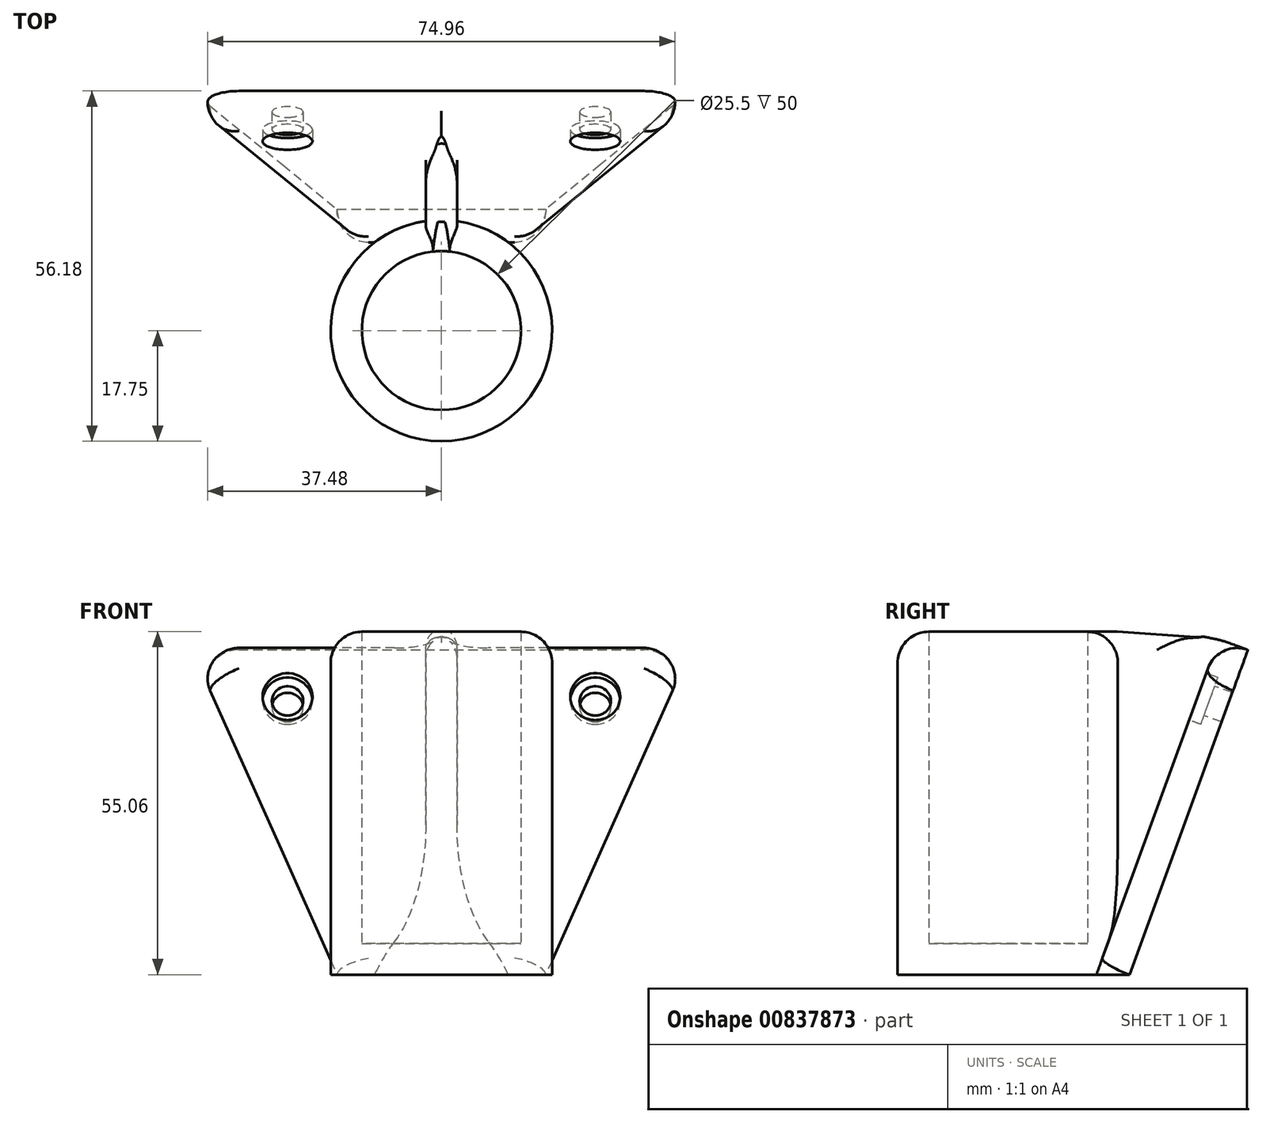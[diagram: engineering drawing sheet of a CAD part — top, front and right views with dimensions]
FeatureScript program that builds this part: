
annotation { "Feature Type Name" : "Feature", "Feature Type Description" : "" }
export const myFeature = defineFeature(function(context is Context, id is Id, definition is map)
    precondition{}
    {
        {
            var Q0;
            Q0=qCreatedBy(makeId("Top.planeOp"),FACE);
            var sketch = newSketch(context, id + "F0", { "sketchPlane" : qUnion([Q0])});
            skCircle(sketch, "E0", {"center": v(0, 0) * mm, "radius": 12.75 * mm});
            skCircle(sketch, "E1", {"center": v(0, 0) * mm, "radius": 17.75 * mm});
            skSolve(sketch);
        }
        {
            var Q0;
            Q0=makeQuery(id+"F0.imprint","IMPRINT",FACE,{"disambiguationData":[TD([[makeQuery(id+"F0.imprint","IMPRINT",EDGE,{"derivedFrom":sQuery(id+"F0.wireOp",EDGE,"E0")}),-1.0]])]});
            extrude(context, id + "F1", {"entities" : qUnion([Q0]), "depth" : 50 * mm, "offsetDistance" : 25 * mm});
        }
        {
            var Q0;
            Q0 = qSketchRegion(id + "F0", true);
            var Q1;
            Q1=makeQuery(id+"F0.imprint","IMPRINT",FACE,{"disambiguationData":[TD([[makeQuery(id+"F0.imprint","IMPRINT",EDGE,{"derivedFrom":sQuery(id+"F0.wireOp",EDGE,"E0")}),1.0]])]});
            extrude(context, id + "F2", {"entities" : qUnion([Q0, Q1]), "operationType" : NewBodyOperationType.ADD, "oppositeDirection" : true, "depth" : 5 * mm, "offsetDistance" : 25 * mm});
        }
        {
            var Q0;
            Q0=qCreatedBy(makeId("Right.planeOp"),FACE);
            var sketch = newSketch(context, id + "F3", { "sketchPlane" : qUnion([Q0])});
            skLineSegment(sketch, "E2.bottom", {"start": v(33.73, 48.81) * mm, "end": v(38.43, 47.1) * mm});
            skLineSegment(sketch, "E2.left", {"start": v(33.73, 48.81) * mm, "end": v(14.14, -5) * mm});
            skLineSegment(sketch, "E2.right", {"start": v(38.43, 47.1) * mm, "end": v(19.46, -5) * mm});
            skLineSegment(sketch, "E3", {"start": v(14.14, -5) * mm, "end": v(19.46, -5) * mm});
            skSolve(sketch);
        }
        {
            var Q0;
            Q0 = qSketchRegion(id + "F3", true);
            extrude(context, id + "F4", {"entities" : qUnion([Q0]), "operationType" : NewBodyOperationType.ADD, "oppositeDirection" : true, "depth" : 40 * mm, "offsetDistance" : 25 * mm, "hasSecondDirection" : true, "secondDirectionOppositeDirection" : false, "secondDirectionDepth" : 40 * mm});
        }
        {
            var Q0;
            Q0=qCreatedBy(makeId("Right.planeOp"),FACE);
            var sketch = newSketch(context, id + "F5", { "sketchPlane" : qUnion([Q0])});
            skLineSegment(sketch, "E4", {"start": v(17.47, 50.06) * mm, "end": v(17.47, 2.94) * mm});
            skLineSegment(sketch, "E5", {"start": v(17.47, 2.94) * mm, "end": v(34.07, 48.86) * mm});
            skLineSegment(sketch, "E6", {"start": v(34.07, 48.86) * mm, "end": v(17.47, 50.06) * mm});
            skSolve(sketch);
        }
        {
            var Q0;
            Q0 = qSketchRegion(id + "F5", true);
            extrude(context, id + "F6", {"entities" : qUnion([Q0]), "operationType" : NewBodyOperationType.ADD, "depth" : 2.5 * mm, "offsetDistance" : 25 * mm, "hasSecondDirection" : true, "secondDirectionOppositeDirection" : true, "secondDirectionDepth" : 2.5 * mm});
        }
        {
            var Q0;
            Q0=makeQuery(id+"F4.opExtrude","SWEPT_FACE",FACE,{"disambiguationData":[OSD([sQuery(id+"F3.wireOp",EDGE,"E2.right")])]});
            var sketch = newSketch(context, id + "F7", { "sketchPlane" : qUnion([Q0])});
            skLineSegment(sketch, "E7", {"start": v(-40, 57.4) * mm, "end": v(-16.73, 1.96) * mm});
            skLineSegment(sketch, "E8", {"start": v(-40, 1.96) * mm, "end": v(-40, 57.4) * mm});
            skLineSegment(sketch, "E9.MirrorCS", {"start": v(40, 57.4) * mm, "end": v(16.73, 1.96) * mm});
            skLineSegment(sketch, "E10.MirrorCS", {"start": v(40, 1.96) * mm, "end": v(40, 57.4) * mm});
            skLineSegment(sketch, "E11", {"start": v(-16.73, 1.96) * mm, "end": v(-16.73, -1.57) * mm});
            skLineSegment(sketch, "E12", {"start": v(-16.73, -1.57) * mm, "end": v(-40, -1.57) * mm});
            skLineSegment(sketch, "E13", {"start": v(-40, -1.57) * mm, "end": v(-40, 1.96) * mm});
            skLineSegment(sketch, "E14", {"start": v(16.73, 1.96) * mm, "end": v(16.73, -1.57) * mm});
            skLineSegment(sketch, "E15", {"start": v(16.73, -1.57) * mm, "end": v(40, -1.57) * mm});
            skLineSegment(sketch, "E16", {"start": v(40, -1.57) * mm, "end": v(40, 1.96) * mm});
            skSolve(sketch);
        }
        {
            var Q0;
            Q0 = qSketchRegion(id + "F7", true);
            extrude(context, id + "F8", {"entities" : qUnion([Q0]), "operationType" : NewBodyOperationType.REMOVE, "oppositeDirection" : true, "depth" : 6 * mm, "offsetDistance" : 25 * mm});
        }
        {
            var Q0;
            Q0=makeQuery(id+"F1.opExtrude","CAP_EDGE",EDGE,{"disambiguationData":[OSD([sQuery(id+"F0.wireOp",EDGE,"E1")])],"isStart":false});
            fillet(context, id + "F9", {"entities" : qUnion([Q0]), "radius" : 5 * mm, "tangentPropagation" : true, "allowEdgeOverflow" : false});
        }
        {
            var Q0;
            Q0=makeQuery(id+"F6.opExtrude","CAP_EDGE",EDGE,{"disambiguationData":[OSD([sQuery(id+"F5.wireOp",EDGE,"E6")])],"isStart":false});
            var Q1;
            Q1=makeQuery(id+"F6.opExtrude","CAP_EDGE",EDGE,{"disambiguationData":[OSD([sQuery(id+"F5.wireOp",EDGE,"E6")])],"isStart":true});
            fillet(context, id + "F10", {"entities" : qUnion([Q0, Q1]), "radius" : 2.5 * mm, "tangentPropagation" : true, "allowEdgeOverflow" : false});
        }
        {
            var Q0;
            Q0=makeQuery(id+"F6.boolean.opBoolean","INTERSECT",EDGE,{"derivedFrom":[makeQuery(id+"F4.opExtrude","SWEPT_FACE",FACE,{"disambiguationData":[OSD([sQuery(id+"F3.wireOp",EDGE,"E2.left")])]}),makeQuery(id+"F6.opExtrude","CAP_FACE",FACE,{"disambiguationData":[OSD([sQuery(id+"F5.wireOp",EDGE,"E4"),sQuery(id+"F5.wireOp",EDGE,"E5"),sQuery(id+"F5.wireOp",EDGE,"E6")])],"isStart":true})]});
            var Q1;
            Q1=makeQuery(id+"F6.boolean.opBoolean","INTERSECT",EDGE,{"derivedFrom":[makeQuery(id+"F4.opExtrude","SWEPT_FACE",FACE,{"disambiguationData":[OSD([sQuery(id+"F3.wireOp",EDGE,"E2.left")])]}),makeQuery(id+"F6.opExtrude","CAP_FACE",FACE,{"disambiguationData":[OSD([sQuery(id+"F5.wireOp",EDGE,"E4"),sQuery(id+"F5.wireOp",EDGE,"E5"),sQuery(id+"F5.wireOp",EDGE,"E6")])],"isStart":false})]});
            fillet(context, id + "F11", {"entities" : qUnion([Q0, Q1]), "radius" : 5 * mm, "tangentPropagation" : true, "allowEdgeOverflow" : false});
        }
        {
            var Q0;
            {var subQ3=sQuery(id+"F3.wireOp",EDGE,"E2.left");Q0=makeQuery(id+"F8.boolean.opBoolean","INTERSECT",EDGE,{"derivedFrom":[makeQuery(id+"F6.boolean.opBoolean","SPLIT",FACE,{"disambiguationData":[TD([makeQuery(id+"F6.opExtrude","CAP_FACE",FACE,{"disambiguationData":[OSD([sQuery(id+"F5.wireOp",EDGE,"E4"),sQuery(id+"F5.wireOp",EDGE,"E5"),sQuery(id+"F5.wireOp",EDGE,"E6")])],"isStart":false})])],"derivedFrom":makeQuery(id+"F4.opExtrude","SWEPT_FACE",FACE,{"disambiguationData":[OSD([subQ3])]})}),makeQuery(id+"F8.opExtrude","SWEPT_FACE",FACE,{"disambiguationData":[OSD([sQuery(id+"F7.wireOp",EDGE,"E11")])]})]});}
            var Q1;
            {var subQ3=sQuery(id+"F3.wireOp",EDGE,"E2.left");Q1=makeQuery(id+"F8.boolean.opBoolean","INTERSECT",EDGE,{"derivedFrom":[makeQuery(id+"F6.boolean.opBoolean","SPLIT",FACE,{"disambiguationData":[TD([makeQuery(id+"F6.opExtrude","CAP_FACE",FACE,{"disambiguationData":[OSD([sQuery(id+"F5.wireOp",EDGE,"E4"),sQuery(id+"F5.wireOp",EDGE,"E5"),sQuery(id+"F5.wireOp",EDGE,"E6")])],"isStart":false})])],"derivedFrom":makeQuery(id+"F4.opExtrude","SWEPT_FACE",FACE,{"disambiguationData":[OSD([subQ3])]})}),makeQuery(id+"F8.opExtrude","SWEPT_FACE",FACE,{"disambiguationData":[OSD([sQuery(id+"F7.wireOp",EDGE,"E7")])]})]});}
            var Q2;
            {var subQ3=sQuery(id+"F3.wireOp",EDGE,"E2.left");Q2=makeQuery(id+"F8.boolean.opBoolean","INTERSECT",EDGE,{"derivedFrom":[makeQuery(id+"F6.boolean.opBoolean","SPLIT",FACE,{"disambiguationData":[TD([makeQuery(id+"F6.opExtrude","CAP_FACE",FACE,{"disambiguationData":[OSD([sQuery(id+"F5.wireOp",EDGE,"E4"),sQuery(id+"F5.wireOp",EDGE,"E5"),sQuery(id+"F5.wireOp",EDGE,"E6")])],"isStart":true})])],"derivedFrom":makeQuery(id+"F4.opExtrude","SWEPT_FACE",FACE,{"disambiguationData":[OSD([subQ3])]})}),makeQuery(id+"F8.opExtrude","SWEPT_FACE",FACE,{"disambiguationData":[OSD([sQuery(id+"F7.wireOp",EDGE,"E14")])]})]});}
            var Q3;
            {var subQ3=sQuery(id+"F3.wireOp",EDGE,"E2.left");Q3=makeQuery(id+"F8.boolean.opBoolean","INTERSECT",EDGE,{"derivedFrom":[makeQuery(id+"F6.boolean.opBoolean","SPLIT",FACE,{"disambiguationData":[TD([makeQuery(id+"F6.opExtrude","CAP_FACE",FACE,{"disambiguationData":[OSD([sQuery(id+"F5.wireOp",EDGE,"E4"),sQuery(id+"F5.wireOp",EDGE,"E5"),sQuery(id+"F5.wireOp",EDGE,"E6")])],"isStart":true})])],"derivedFrom":makeQuery(id+"F4.opExtrude","SWEPT_FACE",FACE,{"disambiguationData":[OSD([subQ3])]})}),makeQuery(id+"F8.opExtrude","SWEPT_FACE",FACE,{"disambiguationData":[OSD([sQuery(id+"F7.wireOp",EDGE,"E9.MirrorCS")])]})]});}
            fillet(context, id + "F12", {"entities" : qUnion([Q0, Q1, Q2, Q3]), "radius" : 5 * mm, "tangentPropagation" : true, "allowEdgeOverflow" : false});
        }
        {
            var Q0;
            {var subQ0=sQuery(id+"F3.wireOp",EDGE,"E2.bottom");var subQ1=sQuery(id+"F3.wireOp",EDGE,"E2.left");Q0=makeQuery(id+"F6.boolean.opBoolean","SPLIT",EDGE,{"disambiguationData":[TD([makeQuery(id+"F6.opExtrude","CAP_FACE",FACE,{"disambiguationData":[OSD([sQuery(id+"F5.wireOp",EDGE,"E4"),sQuery(id+"F5.wireOp",EDGE,"E5"),sQuery(id+"F5.wireOp",EDGE,"E6")])],"isStart":true})])],"derivedFrom":makeQuery(id+"F4.opExtrude","SWEPT_EDGE",EDGE,{"disambiguationData":[OSD([subQ0,subQ1])]})});}
            var Q1;
            {var subQ0=sQuery(id+"F3.wireOp",EDGE,"E2.bottom");var subQ1=sQuery(id+"F3.wireOp",EDGE,"E2.left");Q1=makeQuery(id+"F6.boolean.opBoolean","SPLIT",EDGE,{"disambiguationData":[TD([makeQuery(id+"F6.opExtrude","CAP_FACE",FACE,{"disambiguationData":[OSD([sQuery(id+"F5.wireOp",EDGE,"E4"),sQuery(id+"F5.wireOp",EDGE,"E5"),sQuery(id+"F5.wireOp",EDGE,"E6")])],"isStart":false})])],"derivedFrom":makeQuery(id+"F4.opExtrude","SWEPT_EDGE",EDGE,{"disambiguationData":[OSD([subQ0,subQ1])]})});}
            fillet(context, id + "F13", {"entities" : qUnion([Q0, Q1]), "radius" : 5 * mm, "allowEdgeOverflow" : false});
        }
        {
            var Q0;
            {var subQ3=sQuery(id+"F3.wireOp",EDGE,"E2.left");Q0=makeQuery(id+"F6.boolean.opBoolean","SPLIT",FACE,{"disambiguationData":[TD([makeQuery(id+"F6.opExtrude","CAP_FACE",FACE,{"disambiguationData":[OSD([sQuery(id+"F5.wireOp",EDGE,"E4"),sQuery(id+"F5.wireOp",EDGE,"E5"),sQuery(id+"F5.wireOp",EDGE,"E6")])],"isStart":true})])],"derivedFrom":makeQuery(id+"F4.opExtrude","SWEPT_FACE",FACE,{"disambiguationData":[OSD([subQ3])]})});}
            var sketch = newSketch(context, id + "F14", { "sketchPlane" : qUnion([Q0])});
            skPoint(sketch, "E17", {"position": v(-24.67, 47.59) * mm});
            skPoint(sketch, "E18.MirrorP", {"position": v(24.67, 47.59) * mm});
            skSolve(sketch);
        }
        {
            var Q0;
            Q0=sQuery(id+"F14.wireOp",VERTEX,"E17");
            var Q1;
            Q1=sQuery(id+"F14.wireOp",VERTEX,"E18.MirrorP");
            var Q2;
            Q2=makeQuery(id+"F1.opExtrude","SWEPT_BODY",BODY,{"disambiguationData":[OSD([sQuery(id+"F0.wireOp",EDGE,"E0"),sQuery(id+"F0.wireOp",EDGE,"E1")])]});
            hole(context, id + "F15", {"style" : HoleStyle.C_BORE, "endStyle" : HoleEndStyle.THROUGH, "holeDiameter" : 5 * mm, "cBoreDiameter" : 8 * mm, "cBoreDepth" : 2 * mm, "majorDiameter" : 5 * mm, "isTappedThrough" : true, "tappedDepth" : 12 * mm, "tapClearance" : 3, "locations" : qUnion([Q0, Q1]), "scope" : qUnion([Q2])});
        }
        {
            var Q0;
            {var subQ0=sQuery(id+"F3.wireOp",EDGE,"E2.left");var subQ1=sQuery(id+"F3.wireOp",EDGE,"E2.bottom");Q0=makeQuery(id+"F13.opFillet","BLEND_EDGE",EDGE,{"blendedFrom":[makeQuery(id+"F6.boolean.opBoolean","SPLIT",EDGE,{"disambiguationData":[TD([makeQuery(id+"F6.opExtrude","CAP_FACE",FACE,{"disambiguationData":[OSD([sQuery(id+"F5.wireOp",EDGE,"E4"),sQuery(id+"F5.wireOp",EDGE,"E5"),sQuery(id+"F5.wireOp",EDGE,"E6")])],"isStart":true})])],"derivedFrom":makeQuery(id+"F4.opExtrude","SWEPT_EDGE",EDGE,{"disambiguationData":[OSD([subQ1,subQ0])]})}),makeQuery(id+"F12.opFillet","BLEND_FACE",FACE,{"disambiguationData":[OSD([subQ0,sQuery(id+"F7.wireOp",EDGE,"E9.MirrorCS")])]})],"blendedInto":[makeQuery(id+"F12.opFillet","BLEND_FACE",FACE,{"disambiguationData":[OSD([subQ0,sQuery(id+"F7.wireOp",EDGE,"E9.MirrorCS")])]})]});}
            var Q1;
            {var subQ0=sQuery(id+"F3.wireOp",EDGE,"E2.left");var subQ1=sQuery(id+"F3.wireOp",EDGE,"E2.bottom");Q1=makeQuery(id+"F13.opFillet","BLEND_EDGE",EDGE,{"blendedFrom":[makeQuery(id+"F6.boolean.opBoolean","SPLIT",EDGE,{"disambiguationData":[TD([makeQuery(id+"F6.opExtrude","CAP_FACE",FACE,{"disambiguationData":[OSD([sQuery(id+"F5.wireOp",EDGE,"E4"),sQuery(id+"F5.wireOp",EDGE,"E5"),sQuery(id+"F5.wireOp",EDGE,"E6")])],"isStart":false})])],"derivedFrom":makeQuery(id+"F4.opExtrude","SWEPT_EDGE",EDGE,{"disambiguationData":[OSD([subQ1,subQ0])]})}),makeQuery(id+"F12.opFillet","BLEND_FACE",FACE,{"disambiguationData":[OSD([subQ0,sQuery(id+"F7.wireOp",EDGE,"E7")])]})],"blendedInto":[makeQuery(id+"F12.opFillet","BLEND_FACE",FACE,{"disambiguationData":[OSD([subQ0,sQuery(id+"F7.wireOp",EDGE,"E7")])]})]});}
            fillet(context, id + "F16", {"entities" : qUnion([Q0, Q1]), "radius" : 5 * mm, "tangentPropagation" : true, "allowEdgeOverflow" : false});
        }
    });
